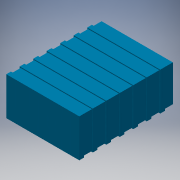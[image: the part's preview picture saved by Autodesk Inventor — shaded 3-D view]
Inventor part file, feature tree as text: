
AUTODESK INVENTOR PART (.ipt)
format: ipt  version: 2019 (Build 230136000, 136)  size: 290,816 bytes
history: native  units: mm
features: extrude x5, sketch x5
ambient origin geometry x8: Origin, YZ Plane, XZ Plane, XY Plane, X Axis, Y Axis, Z Axis, Center Point
bodies: Solid1 (feature_tree)
feature tree (10):
  extrude  "Extrusion1"  Depth=64.8mm
  sketch  "Sketch2"  dims[d3=161.0mm d4=0.0mm]
  extrude  "Extrusion2"  TaperAngle=0.0deg  [1 undecoded]
  extrude  "Extrusion3"  Depth=15.0mm
  sketch  "Sketch5"  dims[d7=8.0mm d8=15.0mm]
  extrude  "Extrusion4"  Depth=15.0mm
  extrude  "Extrusion5"  Depth=15.0mm
  sketch  "Sketch1"  dims[d0=124.5mm d2=64.8mm]
  sketch  "Sketch3"  dims[d5=8.0mm d6=15.0mm]
  sketch  "Sketch6"  dims[d9=8.0mm d10=15.0mm d11=8.0mm d12=15.0mm d13=8.0mm d14=8.0mm d15=15.0mm d16=15.0mm d17=8.0mm d18=15.0mm d19=8.0mm d20=15.0mm d21=8.0mm d22=15.0mm d23=8.0mm d24=15.0mm d25=8.0mm d26=15.0mm d27=8.0mm d28=8.0mm d29=15.0mm d30=15.0mm d31=8.0mm d32=15.0mm d36=1.5mm d37=0.0mm d38=1.5mm d39=0.0mm d40=1.5mm d41=0.0mm d42=1.5mm d43=0.0mm]
note: 1 required parameter value undecoded (feature->parameter linkage not recoverable at this tier; creation-order binding heuristic only, values carry confidence <= 0.55)
